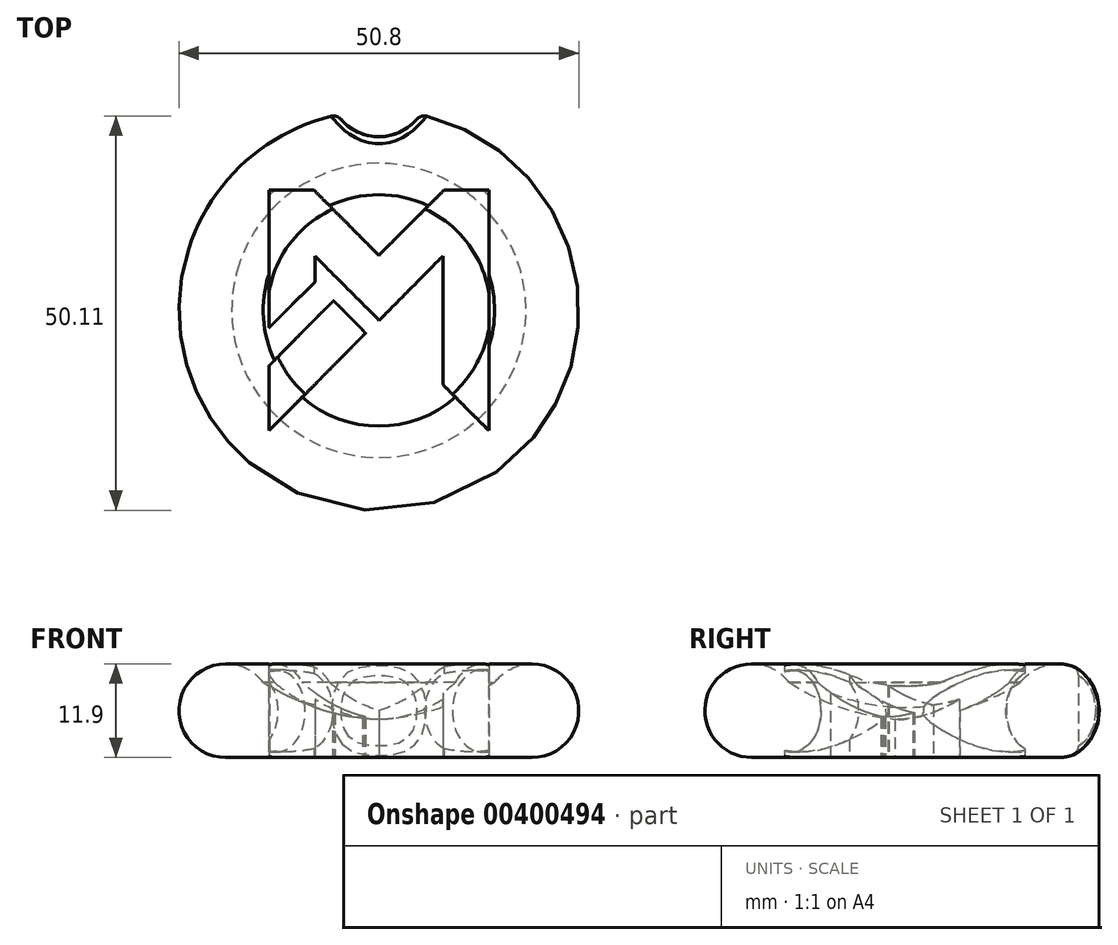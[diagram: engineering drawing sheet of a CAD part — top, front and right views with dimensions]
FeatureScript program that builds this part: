
annotation { "Feature Type Name" : "Feature", "Feature Type Description" : "" }
export const myFeature = defineFeature(function(context is Context, id is Id, definition is map)
    precondition{}
    {
        {
            var Q0;
            Q0=qCreatedBy(makeId("Front.planeOp"),FACE);
            var sketch = newSketch(context, id + "F0", { "sketchPlane" : qUnion([Q0])});
            skCircle(sketch, "E0", {"center": v(-19.45, 5.9) * mm, "radius": 5.95 * mm});
            skPoint(sketch, "E0.first.point", {"position": v(-18.7, 0) * mm});
            skPoint(sketch, "E0.second.point", {"position": v(-22.28, 11.14) * mm});
            skPoint(sketch, "E0.third.point", {"position": v(-14.6, 9.35) * mm});
            skLineSegment(sketch, "E1", {"start": v(0, 0) * mm, "end": v(0, 4.74) * mm});
            skLineSegment(sketch, "E2", {"start": v(-18.7, 0) * mm, "end": v(0, 0) * mm});
            skArc(sketch, "E3", {"start": v(-17.54, 11.54) * mm, "mid": v(-9.3, 6.76) * mm, "end": v(0, 4.74) * mm});
            skSolve(sketch);
        }
        {
            var Q0;
            Q0 = qSketchRegion(id + "F0", true);
            var Q1;
            Q1=sQuery(id+"F0.wireOp",EDGE,"E1");
            revolve(context, id + "F1", {"entities" : qUnion([Q0]), "axis" : qUnion([Q1]), "revolveType" : RevolveType.FULL});
        }
        {
            var Q0;
            Q0=qCreatedBy(makeId("Top.planeOp"),FACE);
            var sketch = newSketch(context, id + "F2", { "sketchPlane" : qUnion([Q0])});
            skLineSegment(sketch, "E4", {"start": v(-13.97, 6.55) * mm, "end": v(-13.97, 6.12) * mm});
            skLineSegment(sketch, "E5", {"start": v(-13.97, 6.12) * mm, "end": v(-13.97, 4.8) * mm});
            skLineSegment(sketch, "E6", {"start": v(-13.97, 4.8) * mm, "end": v(-13.97, 3.17) * mm});
            skLineSegment(sketch, "E7", {"start": v(-13.97, 3.17) * mm, "end": v(-13.96, 1.7) * mm});
            skLineSegment(sketch, "E8", {"start": v(-13.96, 1.7) * mm, "end": v(-13.96, 0.4) * mm});
            skLineSegment(sketch, "E9", {"start": v(-13.96, 0.4) * mm, "end": v(-13.96, -0.66) * mm});
            skLineSegment(sketch, "E10", {"start": v(-13.96, -0.66) * mm, "end": v(-13.95, -1.47) * mm});
            skLineSegment(sketch, "E11", {"start": v(-13.95, -1.47) * mm, "end": v(-13.94, -1.98) * mm});
            skLineSegment(sketch, "E12", {"start": v(-13.94, -1.98) * mm, "end": v(-13.94, -2.16) * mm});
            skLineSegment(sketch, "E13", {"start": v(-13.94, -2.16) * mm, "end": v(-13.94, -2.16) * mm});
            skLineSegment(sketch, "E14", {"start": v(-13.94, -2.16) * mm, "end": v(-13.92, -2.16) * mm});
            skLineSegment(sketch, "E15", {"start": v(-13.92, -2.16) * mm, "end": v(-13.87, -2.1) * mm});
            skLineSegment(sketch, "E16", {"start": v(-13.87, -2.1) * mm, "end": v(-13.7, -1.93) * mm});
            skLineSegment(sketch, "E17", {"start": v(-13.7, -1.93) * mm, "end": v(-13.43, -1.66) * mm});
            skLineSegment(sketch, "E18", {"start": v(-13.43, -1.66) * mm, "end": v(-13.07, -1.3) * mm});
            skLineSegment(sketch, "E19", {"start": v(-13.07, -1.3) * mm, "end": v(-12.64, -0.87) * mm});
            skLineSegment(sketch, "E20", {"start": v(-12.64, -0.87) * mm, "end": v(-12.14, -0.38) * mm});
            skLineSegment(sketch, "E21", {"start": v(-12.14, -0.38) * mm, "end": v(-11.6, 0.16) * mm});
            skLineSegment(sketch, "E22", {"start": v(-11.6, 0.16) * mm, "end": v(-11.17, 0.6) * mm});
            skLineSegment(sketch, "E23", {"start": v(-11.17, 0.6) * mm, "end": v(-11.02, 0.74) * mm});
            skLineSegment(sketch, "E24", {"start": v(-11.02, 0.74) * mm, "end": v(-8.14, 3.64) * mm});
            skLineSegment(sketch, "E25", {"start": v(-8.14, 3.64) * mm, "end": v(-8.14, 6.92) * mm});
            skLineSegment(sketch, "E26", {"start": v(-8.14, 6.92) * mm, "end": v(0.04, -1.25) * mm});
            skLineSegment(sketch, "E27", {"start": v(0.04, -1.25) * mm, "end": v(4.08, 2.83) * mm});
            skLineSegment(sketch, "E28", {"start": v(4.08, 2.83) * mm, "end": v(8.13, 6.92) * mm});
            skLineSegment(sketch, "E29", {"start": v(8.13, 6.92) * mm, "end": v(8.13, -1.25) * mm});
            skLineSegment(sketch, "E30", {"start": v(8.13, -1.25) * mm, "end": v(8.14, -9.43) * mm});
            skLineSegment(sketch, "E31", {"start": v(8.14, -9.43) * mm, "end": v(13.97, -15.26) * mm});
            skLineSegment(sketch, "E32", {"start": v(13.97, -15.26) * mm, "end": v(13.97, 15.26) * mm});
            skLineSegment(sketch, "E33", {"start": v(13.97, 15.26) * mm, "end": v(8.26, 15.26) * mm});
            skLineSegment(sketch, "E34", {"start": v(8.26, 15.26) * mm, "end": v(4.13, 11.14) * mm});
            skLineSegment(sketch, "E35", {"start": v(4.13, 11.14) * mm, "end": v(0, 7) * mm});
            skLineSegment(sketch, "E36", {"start": v(0, 7) * mm, "end": v(-4.12, 11.14) * mm});
            skLineSegment(sketch, "E37", {"start": v(-4.12, 11.14) * mm, "end": v(-8.23, 15.26) * mm});
            skLineSegment(sketch, "E38", {"start": v(-8.23, 15.26) * mm, "end": v(-13.97, 15.26) * mm});
            skLineSegment(sketch, "E39", {"start": v(-13.97, 15.26) * mm, "end": v(-13.97, 6.55) * mm});
            skLineSegment(sketch, "E40", {"start": v(-9.9, -2.91) * mm, "end": v(-13.96, -7.05) * mm});
            skLineSegment(sketch, "E41", {"start": v(-13.96, -7.05) * mm, "end": v(-13.96, -15.26) * mm});
            skLineSegment(sketch, "E42", {"start": v(-13.96, -15.26) * mm, "end": v(-7.84, -9.1) * mm});
            skLineSegment(sketch, "E43", {"start": v(-7.84, -9.1) * mm, "end": v(-7.53, -8.8) * mm});
            skLineSegment(sketch, "E44", {"start": v(-7.53, -8.8) * mm, "end": v(-6.61, -7.87) * mm});
            skLineSegment(sketch, "E45", {"start": v(-6.61, -7.87) * mm, "end": v(-5.47, -6.71) * mm});
            skLineSegment(sketch, "E46", {"start": v(-5.47, -6.71) * mm, "end": v(-4.43, -5.66) * mm});
            skLineSegment(sketch, "E47", {"start": v(-4.43, -5.66) * mm, "end": v(-3.52, -4.74) * mm});
            skLineSegment(sketch, "E48", {"start": v(-3.52, -4.74) * mm, "end": v(-2.77, -3.98) * mm});
            skLineSegment(sketch, "E49", {"start": v(-2.77, -3.98) * mm, "end": v(-2.2, -3.4) * mm});
            skLineSegment(sketch, "E50", {"start": v(-2.2, -3.4) * mm, "end": v(-1.85, -3.02) * mm});
            skLineSegment(sketch, "E51", {"start": v(-1.85, -3.02) * mm, "end": v(-1.73, -2.92) * mm});
            skLineSegment(sketch, "E52", {"start": v(-1.73, -2.92) * mm, "end": v(-1.73, -2.88) * mm});
            skLineSegment(sketch, "E53", {"start": v(-1.73, -2.88) * mm, "end": v(-1.73, -2.86) * mm});
            skLineSegment(sketch, "E54", {"start": v(-1.73, -2.86) * mm, "end": v(-1.77, -2.82) * mm});
            skLineSegment(sketch, "E55", {"start": v(-1.77, -2.82) * mm, "end": v(-1.9, -2.68) * mm});
            skLineSegment(sketch, "E56", {"start": v(-1.9, -2.68) * mm, "end": v(-2.1, -2.47) * mm});
            skLineSegment(sketch, "E57", {"start": v(-2.1, -2.47) * mm, "end": v(-2.34, -2.2) * mm});
            skLineSegment(sketch, "E58", {"start": v(-2.34, -2.2) * mm, "end": v(-2.64, -1.9) * mm});
            skLineSegment(sketch, "E59", {"start": v(-2.64, -1.9) * mm, "end": v(-2.98, -1.55) * mm});
            skLineSegment(sketch, "E60", {"start": v(-2.98, -1.55) * mm, "end": v(-3.34, -1.18) * mm});
            skLineSegment(sketch, "E61", {"start": v(-3.34, -1.18) * mm, "end": v(-3.7, -0.8) * mm});
            skLineSegment(sketch, "E62", {"start": v(-3.7, -0.8) * mm, "end": v(-4.08, -0.42) * mm});
            skLineSegment(sketch, "E63", {"start": v(-4.08, -0.42) * mm, "end": v(-4.44, -0.06) * mm});
            skLineSegment(sketch, "E64", {"start": v(-4.44, -0.06) * mm, "end": v(-4.79, 0.28) * mm});
            skLineSegment(sketch, "E65", {"start": v(-4.79, 0.28) * mm, "end": v(-5.1, 0.59) * mm});
            skLineSegment(sketch, "E66", {"start": v(-5.1, 0.59) * mm, "end": v(-5.36, 0.84) * mm});
            skLineSegment(sketch, "E67", {"start": v(-5.36, 0.84) * mm, "end": v(-5.56, 1.04) * mm});
            skLineSegment(sketch, "E68", {"start": v(-5.56, 1.04) * mm, "end": v(-5.7, 1.17) * mm});
            skLineSegment(sketch, "E69", {"start": v(-5.7, 1.17) * mm, "end": v(-5.75, 1.21) * mm});
            skLineSegment(sketch, "E70", {"start": v(-5.75, 1.21) * mm, "end": v(-5.76, 1.21) * mm});
            skLineSegment(sketch, "E71", {"start": v(-5.76, 1.21) * mm, "end": v(-5.78, 1.21) * mm});
            skLineSegment(sketch, "E72", {"start": v(-5.78, 1.21) * mm, "end": v(-5.86, 1.13) * mm});
            skLineSegment(sketch, "E73", {"start": v(-5.86, 1.13) * mm, "end": v(-6.1, 0.89) * mm});
            skLineSegment(sketch, "E74", {"start": v(-6.1, 0.89) * mm, "end": v(-6.5, 0.5) * mm});
            skLineSegment(sketch, "E75", {"start": v(-6.5, 0.5) * mm, "end": v(-7, 0) * mm});
            skLineSegment(sketch, "E76", {"start": v(-7, 0) * mm, "end": v(-7.6, -0.61) * mm});
            skLineSegment(sketch, "E77", {"start": v(-7.6, -0.61) * mm, "end": v(-8.3, -1.31) * mm});
            skLineSegment(sketch, "E78", {"start": v(-8.3, -1.31) * mm, "end": v(-9.07, -2.08) * mm});
            skLineSegment(sketch, "E79", {"start": v(-9.07, -2.08) * mm, "end": v(-9.69, -2.7) * mm});
            skLineSegment(sketch, "E80", {"start": v(-9.69, -2.7) * mm, "end": v(-9.9, -2.91) * mm});
            skSolve(sketch);
        }
        {
            var Q0;
            Q0=makeQuery(id+"F2.imprint","IMPRINT",FACE,{"disambiguationData":[TD([[makeQuery(id+"F2.imprint","IMPRINT",EDGE,{"derivedFrom":sQuery(id+"F2.wireOp",EDGE,"E4")}),1.0]])]});
            var Q1;
            Q1=makeQuery(id+"F2.imprint","IMPRINT",FACE,{"disambiguationData":[TD([[makeQuery(id+"F2.imprint","IMPRINT",EDGE,{"derivedFrom":sQuery(id+"F2.wireOp",EDGE,"E40")}),1.0]])]});
            extrude(context, id + "F3", {"entities" : qUnion([Q0, Q1]), "operationType" : NewBodyOperationType.REMOVE, "endBound" : BoundingType.THROUGH_ALL, "depth" : 29.2 * mm});
        }
        {
            var Q0;
            Q0=qCreatedBy(makeId("Front.planeOp"),FACE);
            var sketch = newSketch(context, id + "F4", { "sketchPlane" : qUnion([Q0])});
            skCircle(sketch, "E81", {"center": v(-19.34, 5.86) * mm, "radius": 5.2 * mm});
            skSolve(sketch);
        }
        {
            var Q0;
            Q0 = qSketchRegion(id + "F4", true);
            var Q1;
            Q1=sQuery(id+"F0.wireOp",EDGE,"E1");
            revolve(context, id + "F5", {"operationType" : NewBodyOperationType.ADD, "entities" : qUnion([Q0]), "axis" : qUnion([Q1]), "revolveType" : RevolveType.FULL});
        }
        {
            var Q0;
            Q0=qCreatedBy(makeId("Top.planeOp"),FACE);
            var sketch = newSketch(context, id + "F6", { "sketchPlane" : qUnion([Q0])});
            skCircle(sketch, "E82", {"center": v(0, 28.33) * mm, "radius": 6.28 * mm});
            skSolve(sketch);
        }
        {
            var Q0;
            Q0 = qSketchRegion(id + "F6", true);
            extrude(context, id + "F7", {"entities" : qUnion([Q0]), "operationType" : NewBodyOperationType.REMOVE, "endBound" : BoundingType.THROUGH_ALL, "depth" : 25.4 * mm});
        }
        {
            var Q0;
            Q0=makeQuery(id+"F7.boolean.opBoolean","INTERSECT",EDGE,{"derivedFrom":[makeQuery(id+"F1.opRevolve","SWEPT_FACE",FACE,{"disambiguationData":[OSD([sQuery(id+"F0.wireOp",EDGE,"E0")])]}),makeQuery(id+"F7.opExtrude","SWEPT_FACE",FACE,{"disambiguationData":[OSD([sQuery(id+"F6.wireOp",EDGE,"E82")])]})]});
            fillet(context, id + "F8", {"entities" : qUnion([Q0]), "radius" : 1.25 * mm, "tangentPropagation" : true, "allowEdgeOverflow" : false});
        }
    });
